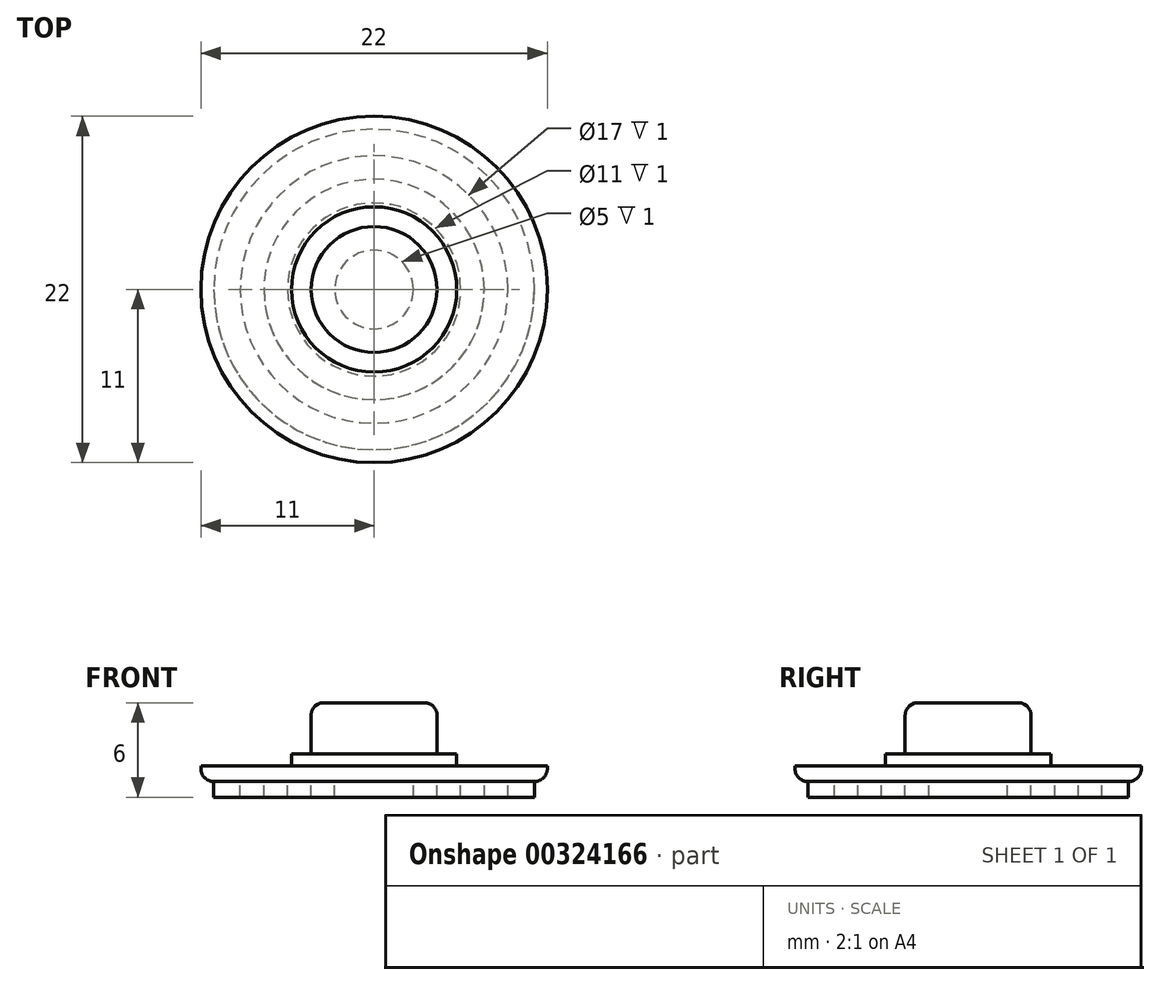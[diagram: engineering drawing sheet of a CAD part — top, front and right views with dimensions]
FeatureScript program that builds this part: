
annotation { "Feature Type Name" : "Feature", "Feature Type Description" : "" }
export const myFeature = defineFeature(function(context is Context, id is Id, definition is map)
    precondition{}
    {
        {
            var Q0;
            Q0=qCreatedBy(makeId("Top.planeOp"),FACE);
            var sketch = newSketch(context, id + "F0", { "sketchPlane" : qUnion([Q0])});
            skCircle(sketch, "E0", {"center": v(0, 0) * mm, "radius": 11 * mm});
            skSolve(sketch);
        }
        {
            var Q0;
            Q0=qSketchRegion(id+"F0",true);
            extrude(context, id + "F1", {"entities" : qUnion([Q0]), "depth" : 1 * mm});
        }
        {
            var Q0;
            Q0=makeQuery(id+"F1.opExtrude","CAP_FACE",FACE,{"disambiguationData":[OSD([sQuery(id+"F0.wireOp",EDGE,"E0")])],"isStart":false});
            var sketch = newSketch(context, id + "F2", { "sketchPlane" : qUnion([Q0])});
            skCircle(sketch, "E1", {"center": v(0, 0) * mm, "radius": 4 * mm});
            skSolve(sketch);
        }
        {
            var Q0;
            Q0=makeQuery(id+"F2.imprint","IMPRINT",FACE,{"disambiguationData":[TD([[makeQuery(id+"F2.imprint","IMPRINT",EDGE,{"derivedFrom":sQuery(id+"F2.wireOp",EDGE,"E1")}),1.0]])]});
            extrude(context, id + "F3", {"entities" : qUnion([Q0]), "operationType" : NewBodyOperationType.ADD, "depth" : 4 * mm});
        }
        {
            var Q0;
            Q0=makeQuery(id+"F1.opExtrude","CAP_EDGE",EDGE,{"disambiguationData":[OSD([sQuery(id+"F0.wireOp",EDGE,"E0")])],"isStart":true});
            var Q1;
            Q1=makeQuery(id+"F3.opExtrude","CAP_EDGE",EDGE,{"disambiguationData":[OSD([sQuery(id+"F2.wireOp",EDGE,"E1")])],"isStart":false});
            fillet(context, id + "F4", {"entities" : qUnion([Q0, Q1]), "radius" : .8 * mm, "tangentPropagation" : true, "allowEdgeOverflow" : false});
        }
        {
            var Q0;
            Q0=makeQuery(id+"F1.opExtrude","CAP_FACE",FACE,{"disambiguationData":[OSD([sQuery(id+"F0.wireOp",EDGE,"E0")])],"isStart":false});
            var sketch = newSketch(context, id + "F5", { "sketchPlane" : qUnion([Q0])});
            skCircle(sketch, "E2", {"center": v(0, 0) * mm, "radius": 5.25 * mm});
            skSolve(sketch);
        }
        {
            var Q0;
            Q0=makeQuery(id+"F5.imprint","IMPRINT",FACE,{"disambiguationData":[TD([[makeQuery(id+"F5.imprint","IMPRINT",EDGE,{"derivedFrom":makeQuery(id+"F3.opExtrude","CAP_EDGE",EDGE,{"disambiguationData":[OSD([sQuery(id+"F2.wireOp",EDGE,"E1")])],"isStart":true})}),1.0]])]});
            var Q1;
            Q1=makeQuery(id+"F5.imprint","IMPRINT",FACE,{"disambiguationData":[TD([[makeQuery(id+"F5.imprint","IMPRINT",EDGE,{"derivedFrom":sQuery(id+"F5.wireOp",EDGE,"E2")}),1.0]])]});
            extrude(context, id + "F6", {"entities" : qUnion([Q0, Q1]), "operationType" : NewBodyOperationType.ADD, "depth" : .75 * mm});
        }
        {
            var Q0;
            Q0=makeQuery(id+"F1.opExtrude","CAP_FACE",FACE,{"disambiguationData":[OSD([sQuery(id+"F0.wireOp",EDGE,"E0")])],"isStart":true});
            var sketch = newSketch(context, id + "F7", { "sketchPlane" : qUnion([Q0])});
            skCircle(sketch, "E3", {"center": v(0, 0) * mm, "radius": 10.18 * mm});
            skCircle(sketch, "E4", {"center": v(0, 0) * mm, "radius": 8.5 * mm});
            skCircle(sketch, "E5", {"center": v(0, 0) * mm, "radius": 7 * mm});
            skCircle(sketch, "E6", {"center": v(0, 0) * mm, "radius": 5.5 * mm});
            skCircle(sketch, "E7", {"center": v(0, 0) * mm, "radius": 4 * mm});
            skCircle(sketch, "E8", {"center": v(0, 0) * mm, "radius": 2.5 * mm});
            skSolve(sketch);
        }
        {
            var Q0;
            Q0=makeQuery(id+"F7.imprint","IMPRINT",FACE,{"disambiguationData":[TD([[makeQuery(id+"F7.imprint","IMPRINT",EDGE,{"derivedFrom":sQuery(id+"F7.wireOp",EDGE,"E5")}),1.0]])]});
            var Q1;
            Q1=makeQuery(id+"F7.imprint","IMPRINT",FACE,{"disambiguationData":[TD([[makeQuery(id+"F7.imprint","IMPRINT",EDGE,{"derivedFrom":sQuery(id+"F7.wireOp",EDGE,"E3")}),1.0]])]});
            var Q2;
            Q2=makeQuery(id+"F7.imprint","IMPRINT",FACE,{"disambiguationData":[TD([[makeQuery(id+"F7.imprint","IMPRINT",EDGE,{"derivedFrom":sQuery(id+"F7.wireOp",EDGE,"E7")}),1.0]])]});
            extrude(context, id + "F8", {"entities" : qUnion([Q0, Q1, Q2]), "operationType" : NewBodyOperationType.ADD, "depth" : 1 * mm});
        }
    });
